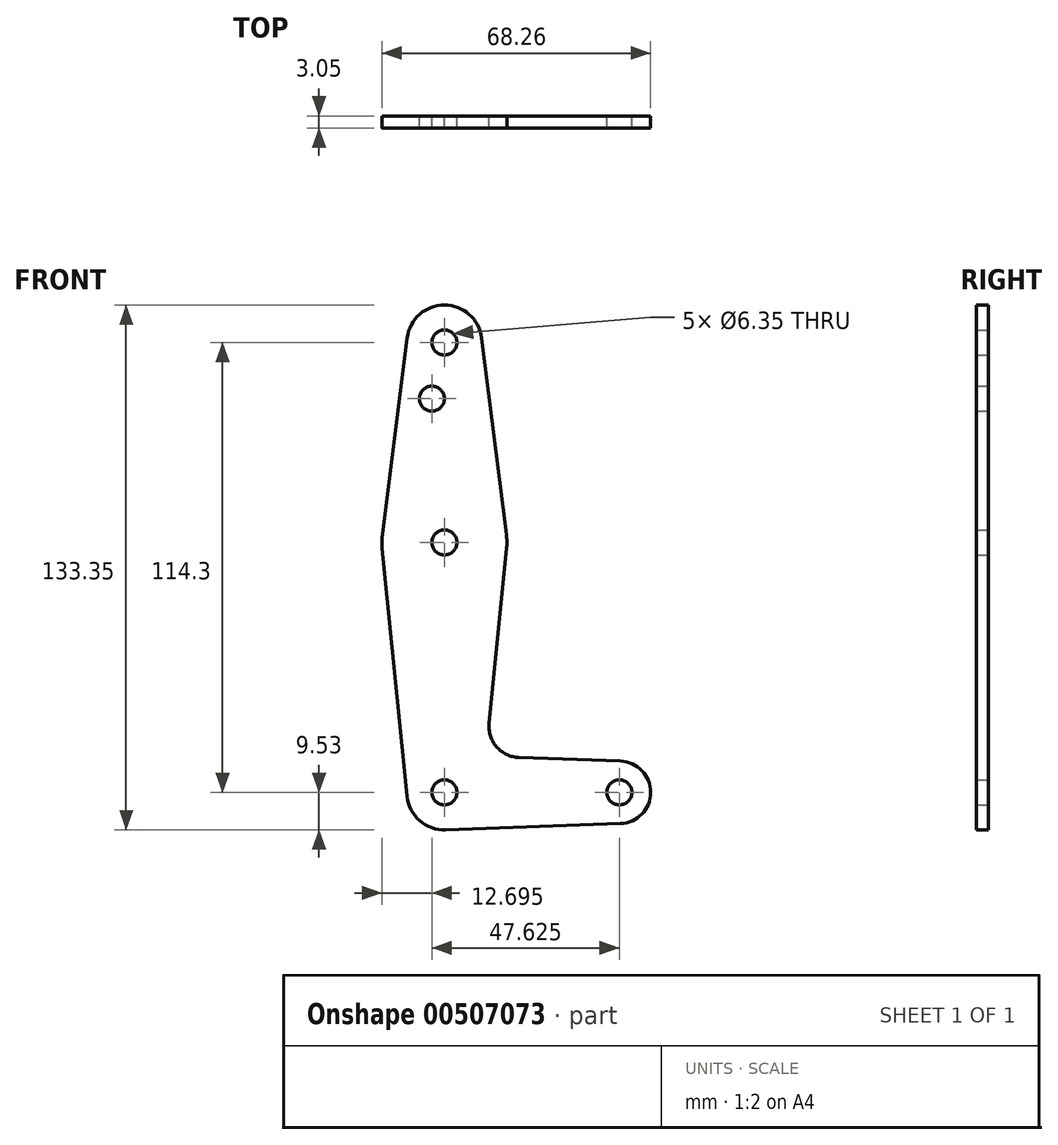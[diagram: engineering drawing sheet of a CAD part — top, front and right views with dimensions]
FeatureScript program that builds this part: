
annotation { "Feature Type Name" : "Feature", "Feature Type Description" : "" }
export const myFeature = defineFeature(function(context is Context, id is Id, definition is map)
    precondition{}
    {
        {
            var Q0;
            Q0=qCreatedBy(makeId("Front.planeOp"),FACE);
            var sketch = newSketch(context, id + "F0", { "sketchPlane" : qUnion([Q0])});
            skCircle(sketch, "E0", {"center": v(0, 0) * mm, "radius": 15.88 * mm});
            skCircle(sketch, "E1", {"center": v(0, 50.8) * mm, "radius": 9.53 * mm});
            skCircle(sketch, "E2", {"center": v(0, -63.5) * mm, "radius": 9.53 * mm});
            skCircle(sketch, "E3", {"center": v(44.45, -63.5) * mm, "radius": 7.94 * mm});
            skLineSegment(sketch, "E4", {"start": v(0, 50.8) * mm, "end": v(0, -63.5) * mm, "construction": true});
            skCircle(sketch, "E5", {"center": v(0, 50.8) * mm, "radius": 3.18 * mm});
            skCircle(sketch, "E6", {"center": v(-3.17, 36.53) * mm, "radius": 3.18 * mm});
            skCircle(sketch, "E7", {"center": v(0, 0) * mm, "radius": 3.18 * mm});
            skCircle(sketch, "E8", {"center": v(0, -63.5) * mm, "radius": 3.18 * mm});
            skCircle(sketch, "E9", {"center": v(44.45, -63.5) * mm, "radius": 3.18 * mm});
            skLineSegment(sketch, "E10", {"start": v(-15.75, 1.98) * mm, "end": v(-9.45, 52) * mm});
            skLineSegment(sketch, "E11", {"start": v(15.75, 1.98) * mm, "end": v(9.45, 52) * mm});
            skLineSegment(sketch, "E12", {"start": v(-9.48, -64.45) * mm, "end": v(-15.8, -1.59) * mm});
            skLineSegment(sketch, "E13", {"start": v(11.34, -45.9) * mm, "end": v(15.8, -1.59) * mm});
            skLineSegment(sketch, "E14", {"start": v(0.34, -73.02) * mm, "end": v(44.73, -71.43) * mm});
            skLineSegment(sketch, "E15", {"start": v(18.97, -54.65) * mm, "end": v(44.73, -55.57) * mm});
            skArc(sketch, "E16.filletArc", {"start": v(11.34, -45.9) * mm, "mid": v(13.26, -51.93) * mm, "end": v(18.97, -54.65) * mm});
            skSolve(sketch);
        }
        {
            var Q0;
            Q0 = qSketchRegion(id + "F0", true);
            extrude(context, id + "F1", {"entities" : qUnion([Q0]), "depth" : 3.05 * mm});
        }
    });
